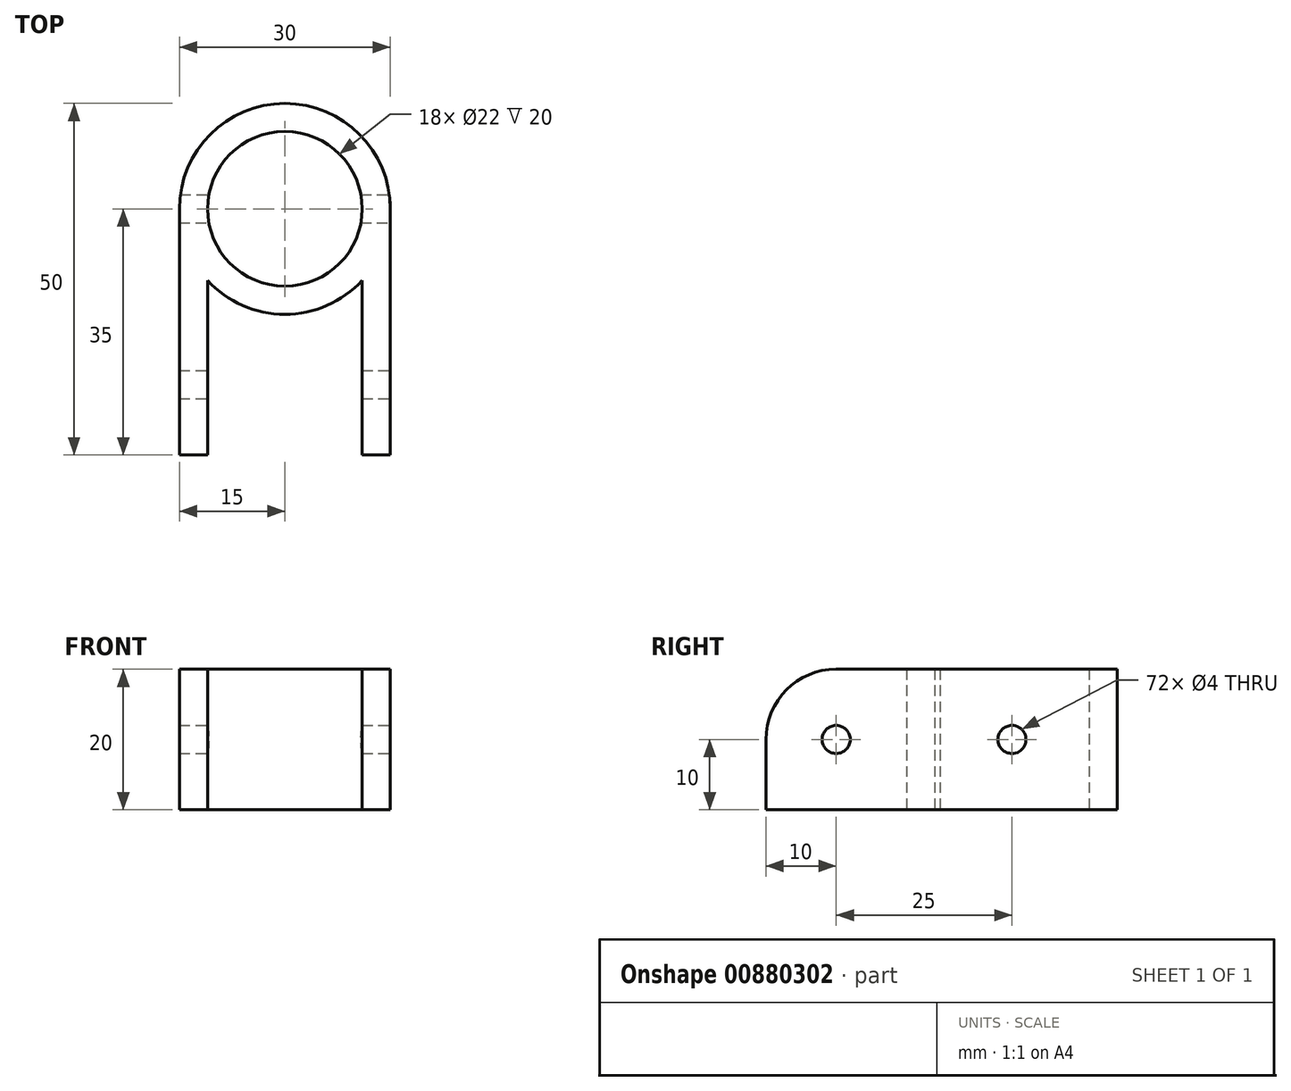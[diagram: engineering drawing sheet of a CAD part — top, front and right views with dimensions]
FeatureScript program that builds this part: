
annotation { "Feature Type Name" : "Feature", "Feature Type Description" : "" }
export const myFeature = defineFeature(function(context is Context, id is Id, definition is map)
    precondition{}
    {
        {
            var Q0;
            Q0=qCreatedBy(makeId("Top.planeOp"),FACE);
            var sketch = newSketch(context, id + "F0", { "sketchPlane" : qUnion([Q0])});
            skCircle(sketch, "E0", {"center": v(0, 0) * mm, "radius": 11 * mm});
            skCircle(sketch, "E1", {"center": v(0, 0) * mm, "radius": 15 * mm});
            skLineSegment(sketch, "E2.bottom", {"start": v(-15, 0) * mm, "end": v(-11, 0) * mm});
            skLineSegment(sketch, "E2.top", {"start": v(-15, -35) * mm, "end": v(-11, -35) * mm});
            skLineSegment(sketch, "E2.left", {"start": v(-15, 0) * mm, "end": v(-15, -35) * mm});
            skLineSegment(sketch, "E2.right", {"start": v(-11, 0) * mm, "end": v(-11, -35) * mm});
            skLineSegment(sketch, "E3.bottom", {"start": v(11, 0) * mm, "end": v(15, 0) * mm});
            skLineSegment(sketch, "E3.top", {"start": v(11, -35) * mm, "end": v(15, -35) * mm});
            skLineSegment(sketch, "E3.left", {"start": v(11, 0) * mm, "end": v(11, -35) * mm});
            skLineSegment(sketch, "E3.right", {"start": v(15, 0) * mm, "end": v(15, -35) * mm});
            skSolve(sketch);
        }
        {
            var Q0;
            {var subQ0=sQuery(id+"F0.wireOp",EDGE,"E2.bottom");Q0=makeQuery(id+"F0.imprint","IMPRINT",FACE,{"disambiguationData":[TD([[makeQuery(id+"F0.imprint","IMPRINT",EDGE,{"derivedFrom":subQ0}),1.0]])]});}
            var Q1;
            {var subQ0=sQuery(id+"F0.wireOp",EDGE,"E3.bottom");Q1=makeQuery(id+"F0.imprint","IMPRINT",FACE,{"disambiguationData":[TD([[makeQuery(id+"F0.imprint","IMPRINT",EDGE,{"derivedFrom":subQ0}),-1.0]])]});}
            var Q2;
            {var subQ0=sQuery(id+"F0.wireOp",EDGE,"E2.bottom");Q2=makeQuery(id+"F0.imprint","IMPRINT",FACE,{"disambiguationData":[TD([[makeQuery(id+"F0.imprint","IMPRINT",EDGE,{"derivedFrom":subQ0}),-1.0]])]});}
            var Q3;
            {var subQ0=sQuery(id+"F0.wireOp",EDGE,"E2.right");var subQ5=sQuery(id+"F0.wireOp",EDGE,"E1");var subQ6=makeQuery(id+"F0.imprint","INTERSECT",VERTEX,{"derivedFrom":[subQ5,subQ0]});Q3=makeQuery(id+"F0.imprint","IMPRINT",FACE,{"disambiguationData":[TD([[makeQuery(id+"F0.imprint","IMPRINT",EDGE,{"disambiguationData":[TD([[subQ6,-1.0]])],"derivedFrom":subQ5}),1.0]])]});}
            var Q4;
            {var subQ4=sQuery(id+"F0.wireOp",EDGE,"E2.top");Q4=makeQuery(id+"F0.imprint","IMPRINT",FACE,{"disambiguationData":[TD([[makeQuery(id+"F0.imprint","IMPRINT",EDGE,{"derivedFrom":subQ4}),1.0]])]});}
            var Q5;
            {var subQ4=sQuery(id+"F0.wireOp",EDGE,"E3.top");Q5=makeQuery(id+"F0.imprint","IMPRINT",FACE,{"disambiguationData":[TD([[makeQuery(id+"F0.imprint","IMPRINT",EDGE,{"derivedFrom":subQ4}),1.0]])]});}
            extrude(context, id + "F1", {"entities" : qUnion([Q0, Q1, Q2, Q3, Q4, Q5]), "depth" : 20 * mm, "offsetDistance" : 25 * mm});
        }
        {
            var Q0;
            Q0=makeQuery(id+"F1.opExtrude","CAP_EDGE",EDGE,{"disambiguationData":[OSD([sQuery(id+"F0.wireOp",EDGE,"E2.top")])],"isStart":false});
            var Q1;
            Q1=makeQuery(id+"F1.opExtrude","CAP_EDGE",EDGE,{"disambiguationData":[OSD([sQuery(id+"F0.wireOp",EDGE,"E3.top")])],"isStart":false});
            fillet(context, id + "F2", {"entities" : qUnion([Q0, Q1]), "radius" : 10 * mm, "tangentPropagation" : true, "allowEdgeOverflow" : false});
        }
        {
            var Q0;
            Q0=makeQuery(id+"F1.opExtrude","SWEPT_FACE",FACE,{"disambiguationData":[OSD([sQuery(id+"F0.wireOp",EDGE,"E3.right")])]});
            var sketch = newSketch(context, id + "F3", { "sketchPlane" : qUnion([Q0])});
            skCircle(sketch, "E4", {"center": v(0, 10) * mm, "radius": 2 * mm});
            skCircle(sketch, "E5", {"center": v(-25, 10) * mm, "radius": 2 * mm});
            skSolve(sketch);
        }
        {
            var Q0;
            Q0=makeQuery(id+"F3.imprint","IMPRINT",FACE,{"disambiguationData":[TD([[makeQuery(id+"F3.imprint","IMPRINT",EDGE,{"derivedFrom":sQuery(id+"F3.wireOp",EDGE,"E5")}),1.0]])]});
            var Q1;
            {var subQ0=sQuery(id+"F3.wireOp",EDGE,"E4");var subQ1=makeQuery(id+"F1.opExtrude","SWEPT_EDGE",EDGE,{"disambiguationData":[OSD([sQuery(id+"F0.wireOp",EDGE,"E1"),sQuery(id+"F0.wireOp",EDGE,"E3.bottom"),sQuery(id+"F0.wireOp",EDGE,"E3.right")])]});var subQ2=makeQuery(id+"F3.imprint","INTERSECT",VERTEX,{"disambiguationData":[OD(0.0)],"derivedFrom":[subQ1,subQ0]});Q1=makeQuery(id+"F3.imprint","IMPRINT",FACE,{"disambiguationData":[TD([[makeQuery(id+"F3.imprint","IMPRINT",EDGE,{"disambiguationData":[TD([[subQ2,-1.0]])],"derivedFrom":subQ0}),1.0]])]});}
            var Q2;
            {var subQ0=sQuery(id+"F3.wireOp",EDGE,"E4");var subQ1=makeQuery(id+"F1.opExtrude","SWEPT_EDGE",EDGE,{"disambiguationData":[OSD([sQuery(id+"F0.wireOp",EDGE,"E1"),sQuery(id+"F0.wireOp",EDGE,"E3.bottom"),sQuery(id+"F0.wireOp",EDGE,"E3.right")])]});var subQ2=makeQuery(id+"F3.imprint","INTERSECT",VERTEX,{"disambiguationData":[OD(0.0)],"derivedFrom":[subQ1,subQ0]});Q2=makeQuery(id+"F3.imprint","IMPRINT",FACE,{"disambiguationData":[TD([[makeQuery(id+"F3.imprint","IMPRINT",EDGE,{"disambiguationData":[TD([[subQ2,1.0]])],"derivedFrom":subQ0}),1.0]])]});}
            extrude(context, id + "F4", {"entities" : qUnion([Q0, Q1, Q2]), "operationType" : NewBodyOperationType.REMOVE, "oppositeDirection" : true, "depth" : 30 * mm, "offsetDistance" : 25 * mm});
        }
    });
